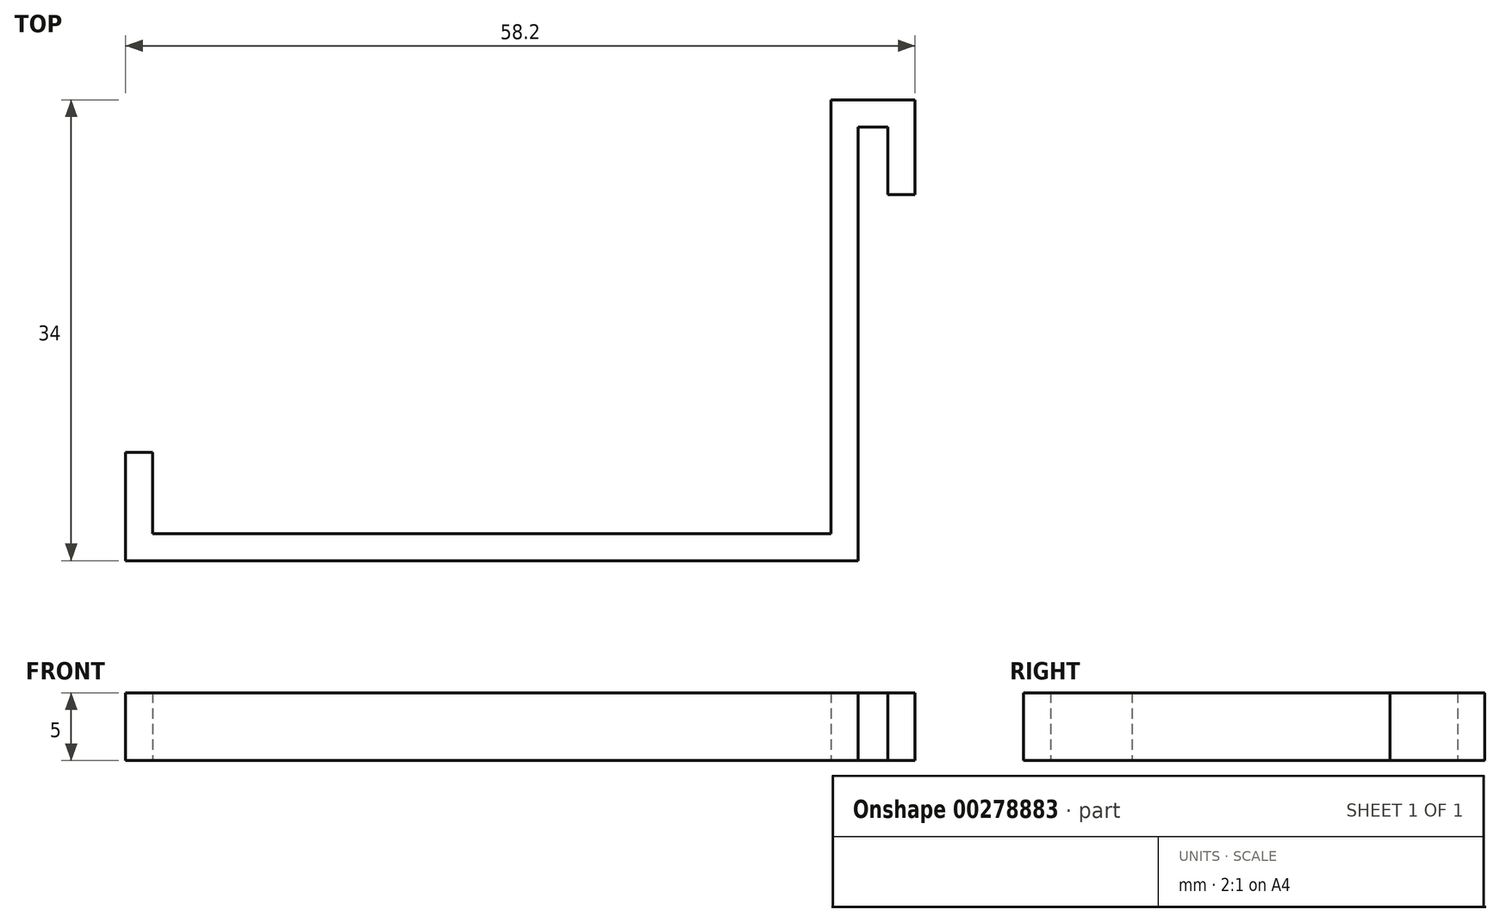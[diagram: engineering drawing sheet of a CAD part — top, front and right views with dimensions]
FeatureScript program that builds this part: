
annotation { "Feature Type Name" : "Feature", "Feature Type Description" : "" }
export const myFeature = defineFeature(function(context is Context, id is Id, definition is map)
    precondition{}
    {
        {
            var Q0;
            Q0=qCreatedBy(makeId("Top.planeOp"),FACE);
            var sketch = newSketch(context, id + "F0", { "sketchPlane" : qUnion([Q0])});
            skLineSegment(sketch, "E0.bottom", {"start": v(25, -1) * mm, "end": v(-25, -1) * mm});
            skLineSegment(sketch, "E0.top", {"start": v(25, 1) * mm, "end": v(-25, 1) * mm});
            skLineSegment(sketch, "E0.left", {"start": v(25, -1) * mm, "end": v(25, 1) * mm, "construction": true});
            skLineSegment(sketch, "E0.right", {"start": v(-25, -1) * mm, "end": v(-25, 1) * mm, "construction": true});
            skPoint(sketch, "E0.middle", {"position": v(0, 0) * mm});
            skLineSegment(sketch, "E1.bottom", {"start": v(-25, -1) * mm, "end": v(-27, -1) * mm});
            skLineSegment(sketch, "E1.top", {"start": v(-25, 7) * mm, "end": v(-27, 7) * mm});
            skLineSegment(sketch, "E1.left", {"start": v(-25, -1) * mm, "end": v(-25, 7) * mm});
            skLineSegment(sketch, "E1.right", {"start": v(-27, -1) * mm, "end": v(-27, 7) * mm});
            skLineSegment(sketch, "E2.bottom", {"start": v(25, -1) * mm, "end": v(27, -1) * mm});
            skLineSegment(sketch, "E2.top", {"start": v(25, 31) * mm, "end": v(27, 31) * mm});
            skLineSegment(sketch, "E2.left", {"start": v(25, -1) * mm, "end": v(25, 31) * mm});
            skLineSegment(sketch, "E2.right", {"start": v(27, -1) * mm, "end": v(27, 31) * mm});
            skLineSegment(sketch, "E3.bottom", {"start": v(25, 31) * mm, "end": v(29.2, 31) * mm});
            skLineSegment(sketch, "E3.top", {"start": v(25, 33) * mm, "end": v(31.2, 33) * mm});
            skLineSegment(sketch, "E3.left", {"start": v(25, 31) * mm, "end": v(25, 33) * mm});
            skLineSegment(sketch, "E3.right", {"start": v(31.2, 31) * mm, "end": v(31.2, 33) * mm});
            skLineSegment(sketch, "E4.bottom", {"start": v(31.2, 31) * mm, "end": v(29.2, 31) * mm, "construction": true});
            skLineSegment(sketch, "E4.top", {"start": v(31.2, 26) * mm, "end": v(29.2, 26) * mm});
            skLineSegment(sketch, "E4.left", {"start": v(31.2, 31) * mm, "end": v(31.2, 26) * mm});
            skLineSegment(sketch, "E4.right", {"start": v(29.2, 31) * mm, "end": v(29.2, 26) * mm});
            skLineSegment(sketch, "E5", {"start": v(27, 31) * mm, "end": v(27, 31) * mm});
            skLineSegment(sketch, "E6", {"start": v(29.2, 31) * mm, "end": v(31.2, 31) * mm, "construction": true});
            skSolve(sketch);
        }
        {
            var Q0;
            Q0 = qSketchRegion(id + "F0", true);
            extrude(context, id + "F1", {"entities" : qUnion([Q0]), "depth" : 5 * mm});
        }
    });
